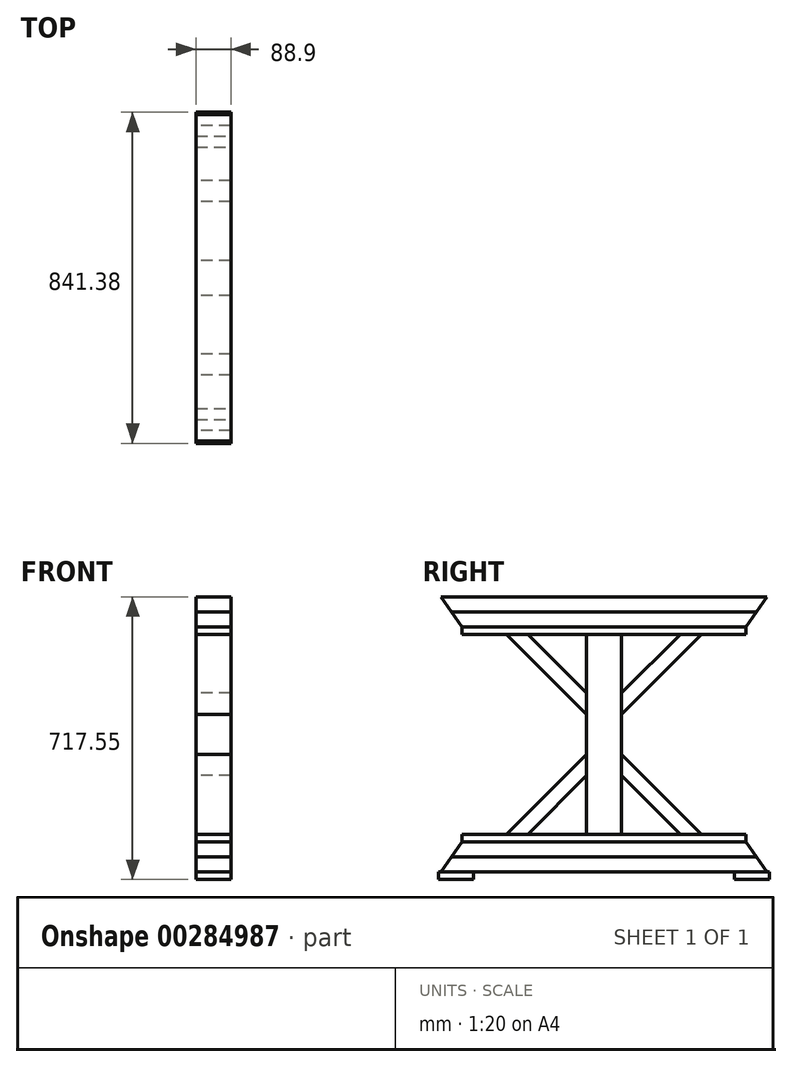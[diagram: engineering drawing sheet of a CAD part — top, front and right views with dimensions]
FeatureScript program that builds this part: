
annotation { "Feature Type Name" : "Feature", "Feature Type Description" : "" }
export const myFeature = defineFeature(function(context is Context, id is Id, definition is map)
    precondition{}
    {
        {
            var Q0;
            Q0=qCreatedBy(makeId("Front.planeOp"),FACE);
            var sketch = newSketch(context, id + "F0", { "sketchPlane" : qUnion([Q0])});
            skLineSegment(sketch, "E0.bottom", {"start": v(0, 0) * mm, "end": v(88.9, 0) * mm});
            skLineSegment(sketch, "E0.top", {"start": v(0, 38.1) * mm, "end": v(88.9, 38.1) * mm});
            skLineSegment(sketch, "E0.left", {"start": v(0, 0) * mm, "end": v(0, 38.1) * mm});
            skLineSegment(sketch, "E0.right", {"start": v(88.9, 0) * mm, "end": v(88.9, 38.1) * mm});
            skSolve(sketch);
        }
        {
            var Q0;
            Q0=makeQuery(id+"F0.imprint","IMPRINT",FACE,{"disambiguationData":[TD([[makeQuery(id+"F0.imprint","IMPRINT",EDGE,{"derivedFrom":sQuery(id+"F0.wireOp",EDGE,"E0.bottom")}),1.0]])]});
            extrude(context, id + "F1", {"entities" : qUnion([Q0]), "endBound" : BoundingType.SYMMETRIC, "depth" : 828.67 * mm});
        }
        {
            var Q0;
            Q0=qCreatedBy(makeId("Front.planeOp"),FACE);
            var sketch = newSketch(context, id + "F2", { "sketchPlane" : qUnion([Q0])});
            skLineSegment(sketch, "E1.bottom", {"start": v(0, 38.1) * mm, "end": v(88.9, 38.1) * mm});
            skLineSegment(sketch, "E1.top", {"start": v(0, 76.2) * mm, "end": v(88.9, 76.2) * mm});
            skLineSegment(sketch, "E1.left", {"start": v(0, 38.1) * mm, "end": v(0, 76.2) * mm});
            skLineSegment(sketch, "E1.right", {"start": v(88.9, 38.1) * mm, "end": v(88.9, 76.2) * mm});
            skSolve(sketch);
        }
        {
            var Q0;
            Q0=makeQuery(id+"F2.imprint","IMPRINT",FACE,{"disambiguationData":[TD([[makeQuery(id+"F2.imprint","IMPRINT",EDGE,{"derivedFrom":sQuery(id+"F2.wireOp",EDGE,"E1.bottom")}),1.0]])]});
            extrude(context, id + "F3", {"entities" : qUnion([Q0]), "endBound" : BoundingType.SYMMETRIC, "depth" : 828.67 * mm});
        }
        {
            var Q0;
            Q0=qCreatedBy(makeId("Front.planeOp"),FACE);
            cPlane(context, id + "F4", {"entities" : qUnion([Q0]), "cplaneType" : CPlaneType.OFFSET, "offset" : 420.7 * mm, "width" : 152.4 * mm, "height" : 152.4 * mm});
        }
        {
            var Q0;
            Q0=qCreatedBy(id+"F4.planeOp",FACE);
            var sketch = newSketch(context, id + "F5", { "sketchPlane" : qUnion([Q0])});
            skLineSegment(sketch, "E2.bottom", {"start": v(0, 0) * mm, "end": v(88.9, 0) * mm});
            skLineSegment(sketch, "E2.top", {"start": v(0, -19.05) * mm, "end": v(88.9, -19.05) * mm});
            skLineSegment(sketch, "E2.left", {"start": v(0, 0) * mm, "end": v(0, -19.05) * mm});
            skLineSegment(sketch, "E2.right", {"start": v(88.9, 0) * mm, "end": v(88.9, -19.05) * mm});
            skSolve(sketch);
        }
        {
            var Q0;
            Q0=makeQuery(id+"F5.imprint","IMPRINT",FACE,{"disambiguationData":[TD([[makeQuery(id+"F5.imprint","IMPRINT",EDGE,{"derivedFrom":sQuery(id+"F5.wireOp",EDGE,"E2.bottom")}),-1.0]])]});
            extrude(context, id + "F6", {"entities" : qUnion([Q0]), "oppositeDirection" : true, "depth" : 88.9 * mm});
        }
        {
            var Q0;
            Q0=makeQuery(id+"F6.opExtrude","SWEPT_BODY",BODY,{"disambiguationData":[OSD([sQuery(id+"F5.wireOp",EDGE,"E2.bottom"),sQuery(id+"F5.wireOp",EDGE,"E2.top"),sQuery(id+"F5.wireOp",EDGE,"E2.left"),sQuery(id+"F5.wireOp",EDGE,"E2.right")])]});
            var Q1;
            Q1=qCreatedBy(makeId("Front.planeOp"),FACE);
            mirror(context, id + "F7", {"entities" : qUnion([Q0]), "mirrorPlane" : qUnion([Q1])});
        }
        {
            var Q0;
            Q0=qCreatedBy(makeId("Front.planeOp"),FACE);
            var sketch = newSketch(context, id + "F8", { "sketchPlane" : qUnion([Q0])});
            skLineSegment(sketch, "E3.bottom", {"start": v(0, 95.25) * mm, "end": v(88.9, 95.25) * mm});
            skLineSegment(sketch, "E3.top", {"start": v(0, 76.2) * mm, "end": v(88.9, 76.2) * mm});
            skLineSegment(sketch, "E3.left", {"start": v(0, 95.25) * mm, "end": v(0, 76.2) * mm});
            skLineSegment(sketch, "E3.right", {"start": v(88.9, 95.25) * mm, "end": v(88.9, 76.2) * mm});
            skSolve(sketch);
        }
        {
            var Q0;
            Q0=makeQuery(id+"F8.imprint","IMPRINT",FACE,{"disambiguationData":[TD([[makeQuery(id+"F8.imprint","IMPRINT",EDGE,{"derivedFrom":sQuery(id+"F8.wireOp",EDGE,"E3.bottom")}),-1.0]])]});
            extrude(context, id + "F9", {"entities" : qUnion([Q0]), "endBound" : BoundingType.SYMMETRIC, "depth" : 720.72 * mm});
        }
        {
            var Q0;
            Q0=makeQuery(id+"F3.opExtrude","SWEPT_FACE",FACE,{"disambiguationData":[OSD([sQuery(id+"F2.wireOp",EDGE,"E1.right")])]});
            var sketch = newSketch(context, id + "F10", { "sketchPlane" : qUnion([Q0])});
            skLineSegment(sketch, "E4", {"start": v(-414.34, 76.2) * mm, "end": v(-414.34, 0) * mm});
            skLineSegment(sketch, "E5", {"start": v(-360.3, 76.2) * mm, "end": v(-414.34, 76.2) * mm});
            skLineSegment(sketch, "E6", {"start": v(-414.34, 0) * mm, "end": v(-360.3, 76.2) * mm});
            skLineSegment(sketch, "E7.MirrorCS", {"start": v(414.34, 0) * mm, "end": v(360.3, 76.2) * mm});
            skLineSegment(sketch, "E8.MirrorCS", {"start": v(414.34, 76.2) * mm, "end": v(414.34, 0) * mm});
            skLineSegment(sketch, "E9.MirrorCS", {"start": v(360.3, 76.2) * mm, "end": v(414.34, 76.2) * mm});
            skSolve(sketch);
        }
        {
            var Q0;
            {var subQ0=sQuery(id+"F10.wireOp",EDGE,"E4");var subQ3=sQuery(id+"F10.wireOp",EDGE,"2tfQZzf6-LnF0-ofD9-kvO9-n6unznoKUB6D");var subQ4=makeQuery(id+"F10.imprint","INTERSECT",VERTEX,{"derivedFrom":[subQ0,subQ3]});Q0=makeQuery(id+"F10.imprint","IMPRINT",FACE,{"disambiguationData":[TD([[makeQuery(id+"F10.imprint","IMPRINT",EDGE,{"disambiguationData":[TD([[subQ4,1.0]])],"derivedFrom":subQ0}),1.0]])]});}
            var Q1;
            {var subQ4=sQuery(id+"F10.wireOp",EDGE,"E5");Q1=makeQuery(id+"F10.imprint","IMPRINT",FACE,{"disambiguationData":[TD([[makeQuery(id+"F10.imprint","IMPRINT",EDGE,{"derivedFrom":subQ4}),-1.0]])]});}
            var Q2;
            {var subQ0=sQuery(id+"F10.wireOp",EDGE,"E9.MirrorCS");Q2=makeQuery(id+"F10.imprint","IMPRINT",FACE,{"disambiguationData":[TD([[makeQuery(id+"F10.imprint","IMPRINT",EDGE,{"derivedFrom":subQ0}),-1.0]])]});}
            var Q3;
            {var subQ0=sQuery(id+"F10.wireOp",EDGE,"E8.MirrorCS");var subQ1=sQuery(id+"F10.wireOp",EDGE,"E7.MirrorCS");var subQ2=makeQuery(id+"F10.imprint","INTERSECT",VERTEX,{"derivedFrom":[subQ1,subQ0]});Q3=makeQuery(id+"F10.imprint","IMPRINT",FACE,{"disambiguationData":[TD([[makeQuery(id+"F10.imprint","IMPRINT",EDGE,{"disambiguationData":[TD([[subQ2,-1.0]])],"derivedFrom":subQ1}),-1.0]])]});}
            var Q4;
            Q4=makeQuery(id+"F3.opExtrude","SWEPT_FACE",FACE,{"disambiguationData":[OSD([sQuery(id+"F2.wireOp",EDGE,"E1.left")])]});
            extrude(context, id + "F11", {"entities" : qUnion([Q0, Q1, Q2, Q3]), "operationType" : NewBodyOperationType.REMOVE, "endBound" : BoundingType.THROUGH_ALL, "oppositeDirection" : true, "endBoundEntityFace" : qUnion([Q4]), "depth" : 25.4 * mm});
        }
        {
            var Q0;
            Q0=makeQuery(id+"F9.opExtrude","SWEPT_FACE",FACE,{"disambiguationData":[OSD([sQuery(id+"F8.wireOp",EDGE,"E3.bottom")])]});
            var sketch = newSketch(context, id + "F12", { "sketchPlane" : qUnion([Q0])});
            skLineSegment(sketch, "E10.bottom", {"start": v(0, 44.45) * mm, "end": v(88.9, 44.45) * mm});
            skLineSegment(sketch, "E10.top", {"start": v(0, -44.45) * mm, "end": v(88.9, -44.45) * mm});
            skLineSegment(sketch, "E10.left", {"start": v(0, 44.45) * mm, "end": v(0, -44.45) * mm});
            skLineSegment(sketch, "E10.right", {"start": v(88.9, 44.45) * mm, "end": v(88.9, -44.45) * mm});
            skSolve(sketch);
        }
        {
            var Q0;
            Q0=makeQuery(id+"F12.imprint","IMPRINT",FACE,{"disambiguationData":[TD([[makeQuery(id+"F12.imprint","IMPRINT",EDGE,{"derivedFrom":sQuery(id+"F12.wireOp",EDGE,"E10.bottom")}),-1.0]])]});
            extrude(context, id + "F13", {"entities" : qUnion([Q0]), "depth" : 508 * mm});
        }
        {
            var Q0;
            Q0=qCreatedBy(makeId("Top.planeOp"),FACE);
            cPlane(context, id + "F14", {"entities" : qUnion([Q0]), "cplaneType" : CPlaneType.OFFSET, "offset" : 349.25 * mm, "width" : 152.4 * mm, "height" : 152.4 * mm});
        }
        {
            var Q0;
            Q0=makeQuery(id+"F9.opExtrude","SWEPT_BODY",BODY,{"disambiguationData":[OSD([sQuery(id+"F8.wireOp",EDGE,"E3.bottom"),sQuery(id+"F8.wireOp",EDGE,"E3.top"),sQuery(id+"F8.wireOp",EDGE,"E3.left"),sQuery(id+"F8.wireOp",EDGE,"E3.right")])]});
            var Q1;
            Q1=makeQuery(id+"F3.opExtrude","SWEPT_BODY",BODY,{"disambiguationData":[OSD([sQuery(id+"F2.wireOp",EDGE,"E1.bottom"),sQuery(id+"F2.wireOp",EDGE,"E1.top"),sQuery(id+"F2.wireOp",EDGE,"E1.left"),sQuery(id+"F2.wireOp",EDGE,"E1.right")])]});
            var Q2;
            Q2=makeQuery(id+"F1.opExtrude","SWEPT_BODY",BODY,{"disambiguationData":[OSD([sQuery(id+"F0.wireOp",EDGE,"E0.bottom"),sQuery(id+"F0.wireOp",EDGE,"E0.top"),sQuery(id+"F0.wireOp",EDGE,"E0.left"),sQuery(id+"F0.wireOp",EDGE,"E0.right")])]});
            var Q3;
            Q3=qCreatedBy(id+"F14.planeOp",FACE);
            mirror(context, id + "F15", {"entities" : qUnion([Q0, Q1, Q2]), "mirrorPlane" : qUnion([Q3])});
        }
        {
            var Q0;
            Q0=makeQuery(id+"F9.opExtrude","SWEPT_FACE",FACE,{"disambiguationData":[OSD([sQuery(id+"F8.wireOp",EDGE,"E3.left")])]});
            var sketch = newSketch(context, id + "F16", { "sketchPlane" : qUnion([Q0])});
            skLineSegment(sketch, "E11", {"start": v(-193.67, 95.25) * mm, "end": v(-44.45, 244.47) * mm});
            skLineSegment(sketch, "E12.0", {"start": v(-247.56, 95.25) * mm, "end": v(-44.45, 298.36) * mm});
            skLineSegment(sketch, "E13", {"start": v(-247.56, 95.25) * mm, "end": v(-193.67, 95.25) * mm});
            skLineSegment(sketch, "E14", {"start": v(-44.45, 298.36) * mm, "end": v(-44.45, 244.47) * mm});
            skSolve(sketch);
        }
        {
            var Q0;
            Q0=makeQuery(id+"F16.imprint","IMPRINT",FACE,{"disambiguationData":[TD([[makeQuery(id+"F16.imprint","IMPRINT",EDGE,{"derivedFrom":sQuery(id+"F16.wireOp",EDGE,"E11")}),1.0]])]});
            extrude(context, id + "F17", {"entities" : qUnion([Q0]), "oppositeDirection" : true, "depth" : 88.9 * mm});
        }
        {
            var Q0;
            Q0=makeQuery(id+"F17.opExtrude","SWEPT_BODY",BODY,{"disambiguationData":[OSD([sQuery(id+"F16.wireOp",EDGE,"E11"),sQuery(id+"F16.wireOp",EDGE,"E12.0"),sQuery(id+"F16.wireOp",EDGE,"E13"),sQuery(id+"F16.wireOp",EDGE,"E14")])]});
            var Q1;
            Q1=qCreatedBy(makeId("Front.planeOp"),FACE);
            mirror(context, id + "F18", {"entities" : qUnion([Q0]), "mirrorPlane" : qUnion([Q1])});
        }
        {
            var Q0;
            Q0=makeQuery(id+"F17.opExtrude","SWEPT_BODY",BODY,{"disambiguationData":[OSD([sQuery(id+"F16.wireOp",EDGE,"E11"),sQuery(id+"F16.wireOp",EDGE,"E12.0"),sQuery(id+"F16.wireOp",EDGE,"E13"),sQuery(id+"F16.wireOp",EDGE,"E14")])]});
            var Q1;
            Q1=makeQuery(id+"F18.opPattern","COPY",BODY,{"derivedFrom":makeQuery(id+"F17.opExtrude","SWEPT_BODY",BODY,{"disambiguationData":[OSD([sQuery(id+"F16.wireOp",EDGE,"E11"),sQuery(id+"F16.wireOp",EDGE,"E12.0"),sQuery(id+"F16.wireOp",EDGE,"E13"),sQuery(id+"F16.wireOp",EDGE,"E14")])]}),"instanceName":"1"});
            var Q2;
            Q2=qCreatedBy(id+"F14.planeOp",FACE);
            mirror(context, id + "F19", {"entities" : qUnion([Q0, Q1]), "mirrorPlane" : qUnion([Q2])});
        }
    });
